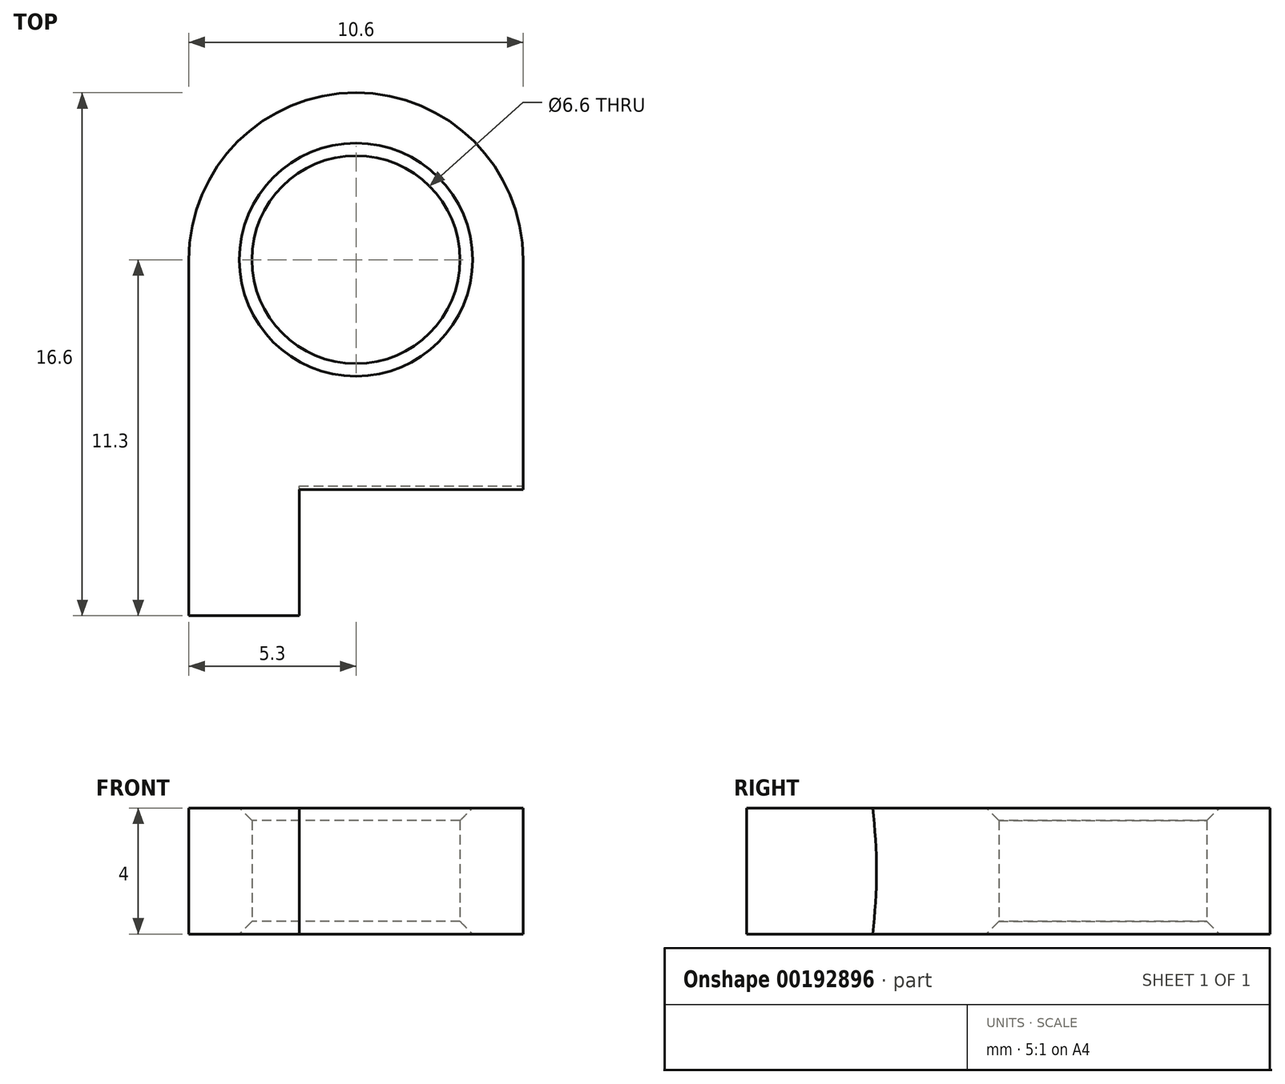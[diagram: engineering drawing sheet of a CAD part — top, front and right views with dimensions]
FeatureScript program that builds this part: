
annotation { "Feature Type Name" : "Feature", "Feature Type Description" : "" }
export const myFeature = defineFeature(function(context is Context, id is Id, definition is map)
    precondition{}
    {
        {
            var Q0;
            Q0=qCreatedBy(makeId("Top.planeOp"),FACE);
            var sketch = newSketch(context, id + "F0", { "sketchPlane" : qUnion([Q0])});
            skCircle(sketch, "E0", {"center": v(0, 0) * mm, "radius": 3.3 * mm});
            skCircle(sketch, "E1", {"center": v(0, 0) * mm, "radius": 5.3 * mm});
            skLineSegment(sketch, "E2.bottom", {"start": v(5.3, -7.3) * mm, "end": v(-5.3, -7.3) * mm});
            skLineSegment(sketch, "E2.top", {"start": v(5.3, 7.3) * mm, "end": v(-5.3, 7.3) * mm});
            skLineSegment(sketch, "E2.left", {"start": v(5.3, -7.3) * mm, "end": v(5.3, 7.3) * mm});
            skLineSegment(sketch, "E2.right", {"start": v(-5.3, -7.3) * mm, "end": v(-5.3, 7.3) * mm});
            skSolve(sketch);
        }
        {
            var Q0;
            Q0=makeQuery(id+"F0.imprint","IMPRINT",FACE,{"disambiguationData":[TD([[makeQuery(id+"F0.imprint","IMPRINT",EDGE,{"derivedFrom":sQuery(id+"F0.wireOp",EDGE,"E0")}),-1.0]])]});
            var Q1;
            {var subQ5=sQuery(id+"F0.wireOp",EDGE,"E2.bottom");Q1=makeQuery(id+"F0.imprint","IMPRINT",FACE,{"disambiguationData":[TD([[makeQuery(id+"F0.imprint","IMPRINT",EDGE,{"derivedFrom":subQ5}),-1.0]])]});}
            extrude(context, id + "F1", {"entities" : qUnion([Q0, Q1]), "depth" : 4 * mm});
        }
        {
            var Q0;
            Q0=makeQuery(id+"F1.opExtrude","SWEPT_FACE",FACE,{"disambiguationData":[OSD([sQuery(id+"F0.wireOp",EDGE,"E2.bottom")])]});
            var sketch = newSketch(context, id + "F2", { "sketchPlane" : qUnion([Q0])});
            skLineSegment(sketch, "E3.bottom", {"start": v(-5.3, 4) * mm, "end": v(-1.8, 4) * mm});
            skLineSegment(sketch, "E3.top", {"start": v(-5.3, 0) * mm, "end": v(-1.8, 0) * mm});
            skLineSegment(sketch, "E3.left", {"start": v(-5.3, 4) * mm, "end": v(-5.3, 0) * mm});
            skLineSegment(sketch, "E3.right", {"start": v(-1.8, 4) * mm, "end": v(-1.8, 0) * mm});
            skSolve(sketch);
        }
        {
            var Q0;
            Q0 = qSketchRegion(id + "F2", true);
            extrude(context, id + "F3", {"entities" : qUnion([Q0]), "operationType" : NewBodyOperationType.ADD, "depth" : 4 * mm});
        }
        {
            var Q0;
            Q0=makeQuery(id+"F1.opExtrude","CAP_EDGE",EDGE,{"disambiguationData":[OSD([sQuery(id+"F0.wireOp",EDGE,"E0")])],"isStart":false});
            var Q1;
            Q1=makeQuery(id+"F1.opExtrude","CAP_EDGE",EDGE,{"disambiguationData":[OSD([sQuery(id+"F0.wireOp",EDGE,"E0")])],"isStart":true});
            chamfer(context, id + "F4", {"entities" : qUnion([Q0, Q1]), "width" : 0.4 * mm, "tangentPropagation" : true});
        }
        {
            var Q0;
            Q0=makeQuery(id+"F1.opExtrude","SWEPT_FACE",FACE,{"disambiguationData":[OSD([sQuery(id+"F0.wireOp",EDGE,"E2.left")])]});
            var sketch = newSketch(context, id + "F5", { "sketchPlane" : qUnion([Q0])});
            skCircle(sketch, "E4", {"center": v(-23.38, 2) * mm, "radius": 16.2 * mm});
            skPoint(sketch, "E4.first.point", {"position": v(-7.3, 4) * mm});
            skPoint(sketch, "E4.second.point", {"position": v(-7.3, 0) * mm});
            skPoint(sketch, "E4.third.point", {"position": v(-27.35, -13.7) * mm});
            skSolve(sketch);
        }
        {
            var Q0;
            Q0 = qSketchRegion(id + "F5", true);
            var Q1;
            Q1=makeQuery(id+"F3.opExtrude","SWEPT_FACE",FACE,{"disambiguationData":[OSD([sQuery(id+"F2.wireOp",EDGE,"E3.right")])]});
            extrude(context, id + "F6", {"entities" : qUnion([Q0]), "operationType" : NewBodyOperationType.REMOVE, "endBound" : BoundingType.UP_TO_SURFACE, "oppositeDirection" : true, "endBoundEntityFace" : qUnion([Q1]), "depth" : 25 * mm});
        }
    });
